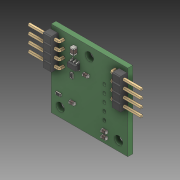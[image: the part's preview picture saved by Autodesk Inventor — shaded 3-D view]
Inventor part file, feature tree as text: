
AUTODESK INVENTOR PART (.ipt)
format: ipt  version: 2020 (Build 240168000, 168)  size: 616,448 bytes
history: native  units: in
note: dims shown in document units (in); Inventor stores cm internally (conversion verified against a paired STEP export)
features: other x12, sketch x1
ambient origin geometry x8: Origin, YZ Plane, XZ Plane, XY Plane, X Axis, Y Axis, Z Axis, Center Point
bodies: Solid1 (feature_tree)
feature tree (13):
  other  "SmallEncoder.iam"
  other  "C_0603_1608Metric.iam:1::SOLID_1.ipt:1"
  other  "C_0603_1608Metric.iam:2::SOLID_1.ipt:1"
  other  "C_0603_1608Metric.iam:3::SOLID_1.ipt:1"
  other  "R_0603_1608Metric.iam:1::SOLID_2.ipt:1"
  other  "R_0603_1608Metric.iam:2::SOLID_2.ipt:1"
  other  "C_0603_1608Metric.iam:4::SOLID_1.ipt:1"
  other  "C_0805_2012Metric.iam:1::SOLID_3.ipt:1"
  other  "PinHeader_1x04_P2.54mm_Horizontal.iam:1::SOLID_4.ipt:1"
  other  "PinHeader_1x04_P2.54mm_Horizontal.iam:2::SOLID_4.ipt:1"
  other  "SOT-23-5.iam:1::SOLID_5.ipt:1"
  other  "COMPOUND.ipt:1"
  sketch  "Sketch1"  dims[d0=0.3937in d1=0.7461in d2=0.748in d3=0.9843in]
